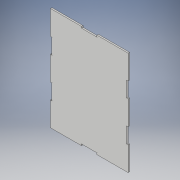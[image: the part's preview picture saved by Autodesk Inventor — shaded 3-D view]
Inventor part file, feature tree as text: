
AUTODESK INVENTOR PART (.ipt)
format: ipt  version: 2017 (Build 210142000, 142)  size: 137,728 bytes
history: native  units: in
note: dims shown in document units (in); Inventor stores cm internally (conversion verified against a paired STEP export)
features: extrude x1, sketch x1
ambient origin geometry x8: Origin, YZ Plane, XZ Plane, XY Plane, X Axis, Y Axis, Z Axis, Center Point
bodies: Solid1 (feature_tree)
feature tree (2):
  extrude  "Extrusion1"  Depth=5.9055in
  sketch  "Sketch1"  dims[d1=7.874in d2=5.9055in d3=2.3622in d4=1.1811in d5=2.3622in d6=0.1181in d26=1.1811in d27=2.3622in d28=2.3622in d29=1.1811in d30=1.1811in d31=0.1181in d32=0.1181in d34=0.1181in d35=0.1181in d36=1.8346in d37=1.8346in d38=1.8346in d39=1.8346in d40=1.8346in d41=1.8346in d42=0.1181in d43=0.0in d44=0.1181in d45=0.1181in d46=0.1181in d47=0.1181in]
